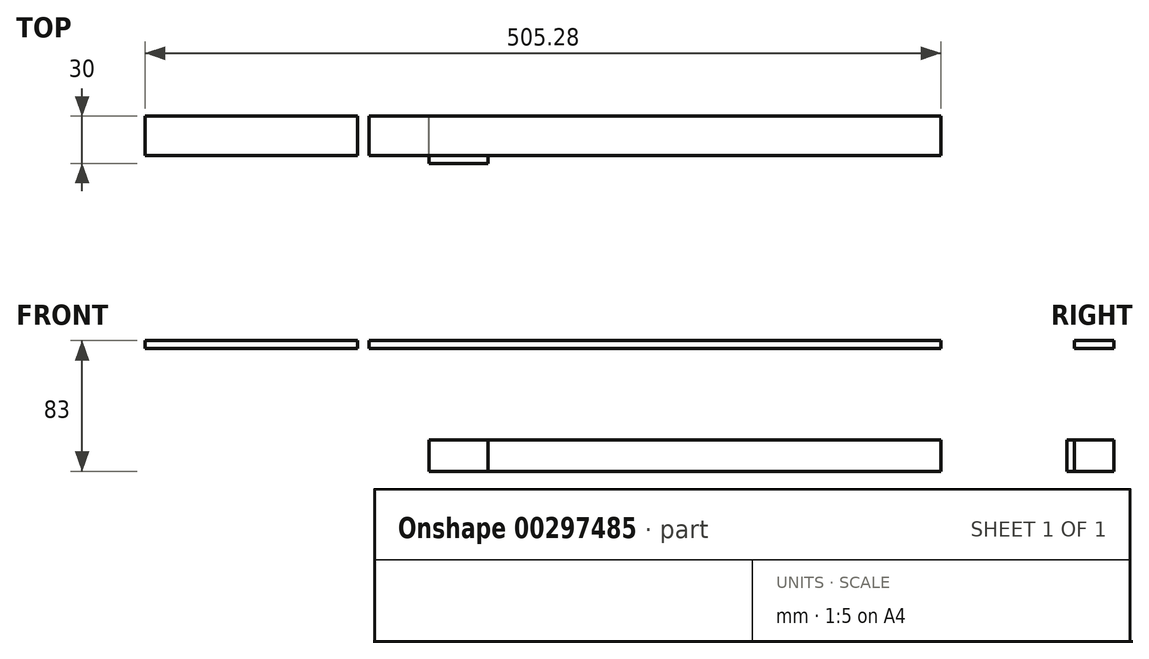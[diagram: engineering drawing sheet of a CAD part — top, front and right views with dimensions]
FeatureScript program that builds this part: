
annotation { "Feature Type Name" : "Feature", "Feature Type Description" : "" }
export const myFeature = defineFeature(function(context is Context, id is Id, definition is map)
    precondition{}
    {
        {
            var Q0;
            Q0=qCreatedBy(makeId("Front.planeOp"),FACE);
            var sketch = newSketch(context, id + "F0", { "sketchPlane" : qUnion([Q0])});
            skLineSegment(sketch, "E0.bottom", {"start": v(0, 0) * mm, "end": v(363, 0) * mm});
            skLineSegment(sketch, "E0.top", {"start": v(0, 5) * mm, "end": v(363, 5) * mm});
            skLineSegment(sketch, "E0.left", {"start": v(0, 0) * mm, "end": v(0, 5) * mm});
            skLineSegment(sketch, "E0.right", {"start": v(363, 0) * mm, "end": v(363, 5) * mm});
            skLineSegment(sketch, "E1.bottom", {"start": v(-7.28, 0) * mm, "end": v(-142.28, 0) * mm});
            skLineSegment(sketch, "E1.top", {"start": v(-7.28, 5) * mm, "end": v(-142.28, 5) * mm});
            skLineSegment(sketch, "E1.left", {"start": v(-7.28, 0) * mm, "end": v(-7.28, 5) * mm});
            skLineSegment(sketch, "E1.right", {"start": v(-142.28, 0) * mm, "end": v(-142.28, 5) * mm});
            skPoint(sketch, "E2", {"position": v(-74.78, 0) * mm});
            skLineSegment(sketch, "E3.bottom", {"start": v(363, -78) * mm, "end": v(18, -78) * mm});
            skLineSegment(sketch, "E3.top", {"start": v(363, -58) * mm, "end": v(18, -58) * mm});
            skLineSegment(sketch, "E3.left", {"start": v(363, -78) * mm, "end": v(363, -58) * mm});
            skLineSegment(sketch, "E3.right", {"start": v(18, -78) * mm, "end": v(18, -58) * mm});
            skLineSegment(sketch, "E4.bottom", {"start": v(18, -58) * mm, "end": v(38, -58) * mm});
            skLineSegment(sketch, "E4.top", {"start": v(18, -78) * mm, "end": v(38, -78) * mm});
            skLineSegment(sketch, "E4.left", {"start": v(18, -58) * mm, "end": v(18, -78) * mm});
            skLineSegment(sketch, "E4.right", {"start": v(38, -58) * mm, "end": v(38, -78) * mm});
            skPoint(sketch, "E5", {"position": v(28, -58) * mm});
            skLineSegment(sketch, "E6.bottom", {"start": v(75.57, -13.18) * mm, "end": v(3.7, -13.18) * mm});
            skLineSegment(sketch, "E6.top", {"start": v(75.57, -93.33) * mm, "end": v(3.7, -93.33) * mm});
            skLineSegment(sketch, "E6.left", {"start": v(75.57, -13.18) * mm, "end": v(75.57, -93.33) * mm});
            skLineSegment(sketch, "E6.right", {"start": v(3.7, -13.18) * mm, "end": v(3.7, -93.33) * mm});
            skCircle(sketch, "E7", {"center": v(8.7, -18.18) * mm, "radius": 1.4 * mm});
            skCircle(sketch, "E8", {"center": v(11.78, -63.82) * mm, "radius": 5 * mm});
            skCircle(sketch, "E9", {"center": v(6.78, -42.82) * mm, "radius": 1.4 * mm});
            skCircle(sketch, "E10", {"center": v(6.78, -84.82) * mm, "radius": 1.4 * mm});
            skCircle(sketch, "E11", {"center": v(16.78, -84.82) * mm, "radius": 1.4 * mm});
            skCircle(sketch, "E12", {"center": v(16.78, -42.82) * mm, "radius": 1.4 * mm});
            skPoint(sketch, "E13", {"position": v(0, 0) * mm});
            skSolve(sketch);
        }
        {
            var Q0;
            {var subQ9=sQuery(id+"F0.wireOp",EDGE,"E4.bottom");Q0=makeQuery(id+"F0.imprint","IMPRINT",FACE,{"disambiguationData":[TD([[makeQuery(id+"F0.imprint","IMPRINT",EDGE,{"derivedFrom":subQ9}),1.0]])]});}
            var Q1;
            Q1=makeQuery(id+"F0.imprint","IMPRINT",FACE,{"disambiguationData":[TD([[makeQuery(id+"F0.imprint","IMPRINT",EDGE,{"derivedFrom":sQuery(id+"F0.wireOp",EDGE,"E4.bottom")}),-1.0]])]});
            var Q2;
            {var subQ0=sQuery(id+"F0.wireOp",EDGE,"E4.right");Q2=makeQuery(id+"F0.imprint","IMPRINT",FACE,{"disambiguationData":[TD([[makeQuery(id+"F0.imprint","IMPRINT",EDGE,{"derivedFrom":subQ0}),1.0]])]});}
            extrude(context, id + "F1", {"entities" : qUnion([Q0, Q1, Q2]), "depth" : 5 * mm});
        }
        {
            var Q0;
            Q0=makeQuery(id+"F0.imprint","IMPRINT",FACE,{"disambiguationData":[TD([[makeQuery(id+"F0.imprint","IMPRINT",EDGE,{"derivedFrom":sQuery(id+"F0.wireOp",EDGE,"E1.bottom")}),-1.0]])]});
            var Q1;
            Q1=makeQuery(id+"F0.imprint","IMPRINT",FACE,{"disambiguationData":[TD([[makeQuery(id+"F0.imprint","IMPRINT",EDGE,{"derivedFrom":sQuery(id+"F0.wireOp",EDGE,"E0.bottom")}),1.0]])]});
            var Q2;
            {var subQ0=sQuery(id+"F0.wireOp",EDGE,"E3.left");Q2=makeQuery(id+"F0.imprint","IMPRINT",FACE,{"disambiguationData":[TD([[makeQuery(id+"F0.imprint","IMPRINT",EDGE,{"derivedFrom":subQ0}),1.0]])]});}
            var Q3;
            {var subQ0=sQuery(id+"F0.wireOp",EDGE,"E4.right");Q3=makeQuery(id+"F0.imprint","IMPRINT",FACE,{"disambiguationData":[TD([[makeQuery(id+"F0.imprint","IMPRINT",EDGE,{"derivedFrom":subQ0}),1.0]])]});}
            var Q4;
            Q4=makeQuery(id+"F0.imprint","IMPRINT",FACE,{"disambiguationData":[TD([[makeQuery(id+"F0.imprint","IMPRINT",EDGE,{"derivedFrom":sQuery(id+"F0.wireOp",EDGE,"E4.bottom")}),-1.0]])]});
            extrude(context, id + "F2", {"entities" : qUnion([Q0, Q1, Q2, Q3, Q4]), "operationType" : NewBodyOperationType.ADD, "oppositeDirection" : true, "depth" : 25 * mm});
        }
    });
